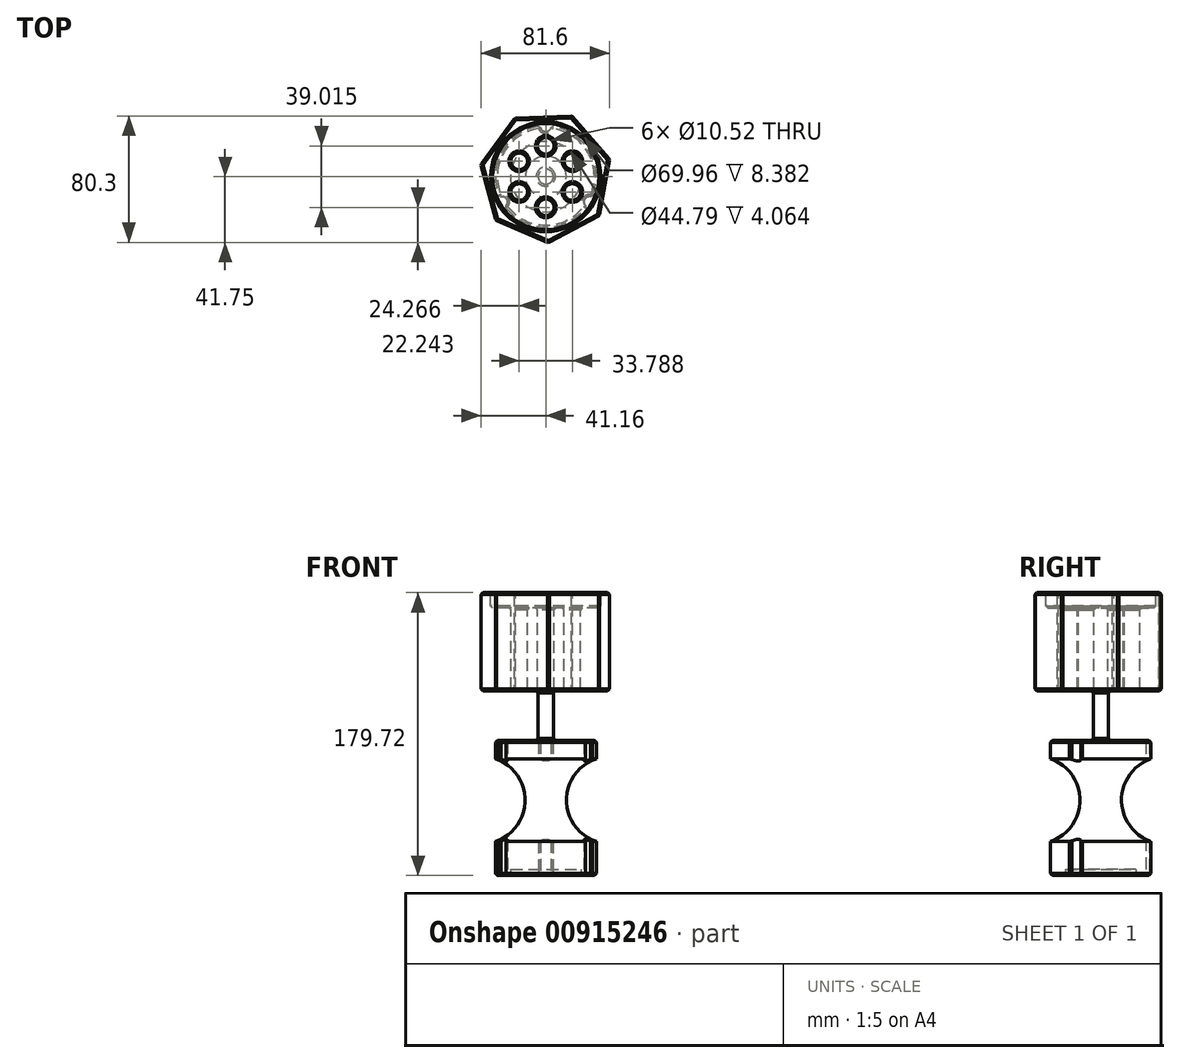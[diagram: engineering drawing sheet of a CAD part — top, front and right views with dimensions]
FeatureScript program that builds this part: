
annotation { "Feature Type Name" : "Feature", "Feature Type Description" : "" }
export const myFeature = defineFeature(function(context is Context, id is Id, definition is map)
    precondition{}
    {
        {
            var Q0;
            Q0=qCreatedBy(makeId("Front.planeOp"),FACE);
            var sketch = newSketch(context, id + "F0", { "sketchPlane" : qUnion([Q0])});
            skLineSegment(sketch, "E0.bottom", {"start": v(0, 38.08) * mm, "end": v(32.08, 38.08) * mm});
            skLineSegment(sketch, "E0.top", {"start": v(0, -47.91) * mm, "end": v(32.08, -47.91) * mm});
            skLineSegment(sketch, "E0.left", {"start": v(0, 38.08) * mm, "end": v(0, -47.91) * mm});
            skLineSegment(sketch, "E0.right", {"start": v(32.08, 38.08) * mm, "end": v(32.08, -47.91) * mm});
            skLineSegment(sketch, "E1", {"start": v(0, 0) * mm, "end": v(0, 52.01) * mm, "construction": true});
            skLineSegment(sketch, "E2", {"start": v(0, 0) * mm, "end": v(0, -67.99) * mm, "construction": true});
            skSolve(sketch);
        }
        {
            var Q0;
            Q0 = qSketchRegion(id + "F0", true);
            var Q1;
            Q1=sQuery(id+"F0.wireOp",EDGE,"E1");
            revolve(context, id + "F1", {"surfaceOperationType" : NewSurfaceOperationType.NEW, "entities" : qUnion([Q0]), "axis" : qUnion([Q1]), "revolveType" : RevolveType.FULL});
        }
        {
            var Q0;
            Q0=makeQuery(id+"F1.opRevolve","SWEPT_FACE",FACE,{"disambiguationData":[OSD([sQuery(id+"F0.wireOp",EDGE,"E0.bottom")])]});
            var sketch = newSketch(context, id + "F2", { "sketchPlane" : qUnion([Q0])});
            skCircle(sketch, "E3", {"center": v(0, 0) * mm, "radius": 4.8 * mm});
            skSolve(sketch);
        }
        {
            var Q0;
            Q0 = qSketchRegion(id + "F2", true);
            extrude(context, id + "F3", {"entities" : qUnion([Q0]), "operationType" : NewBodyOperationType.ADD, "depth" : 93.73 * mm, "offsetDistance" : 25.4 * mm});
        }
        {
            var Q0;
            Q0=makeQuery(id+"F3.opExtrude","CAP_FACE",FACE,{"disambiguationData":[OSD([sQuery(id+"F2.wireOp",EDGE,"E3")])],"isStart":false});
            var sketch = newSketch(context, id + "F4", { "sketchPlane" : qUnion([Q0])});
            skCircle(sketch, "E4.cCircle", {"center": v(0, 0) * mm, "radius": 37.86 * mm, "construction": true});
            skLineSegment(sketch, "E4.0", {"start": v(40.55, 11.03) * mm, "end": v(33.9, -24.83) * mm});
            skLineSegment(sketch, "E4.1", {"start": v(33.9, -24.83) * mm, "end": v(1.73, -41.99) * mm});
            skLineSegment(sketch, "E4.2", {"start": v(1.73, -41.99) * mm, "end": v(-31.75, -27.53) * mm});
            skLineSegment(sketch, "E4.3", {"start": v(-31.75, -27.53) * mm, "end": v(-41.32, 7.66) * mm});
            skLineSegment(sketch, "E4.4", {"start": v(-41.32, 7.66) * mm, "end": v(-19.78, 37.08) * mm});
            skLineSegment(sketch, "E4.5", {"start": v(-19.78, 37.08) * mm, "end": v(16.66, 38.58) * mm});
            skLineSegment(sketch, "E4.6", {"start": v(16.66, 38.58) * mm, "end": v(40.55, 11.03) * mm});
            skPoint(sketch, "E4.0.midPoint", {"position": v(37.23, -6.9) * mm});
            skSolve(sketch);
        }
        {
            var Q0;
            Q0 = qSketchRegion(id + "F4", true);
            extrude(context, id + "F5", {"entities" : qUnion([Q0]), "operationType" : NewBodyOperationType.ADD, "oppositeDirection" : true, "depth" : 62.48 * mm, "offsetDistance" : 25.4 * mm});
        }
        {
            var Q0;
            Q0=makeQuery(id+"F5.boolean.opBoolean","MERGE",FACE,{"derivedFrom":[makeQuery(id+"F3.opExtrude","CAP_FACE",FACE,{"disambiguationData":[OSD([sQuery(id+"F2.wireOp",EDGE,"E3")])],"isStart":false}),makeQuery(id+"F5.opExtrude","CAP_FACE",FACE,{"disambiguationData":[OSD([sQuery(id+"F4.wireOp",EDGE,"E4.0"),sQuery(id+"F4.wireOp",EDGE,"E4.1"),sQuery(id+"F4.wireOp",EDGE,"E4.2"),sQuery(id+"F4.wireOp",EDGE,"E4.3"),sQuery(id+"F4.wireOp",EDGE,"E4.4"),sQuery(id+"F4.wireOp",EDGE,"E4.5"),sQuery(id+"F4.wireOp",EDGE,"E4.6")])],"isStart":true})]});
            var sketch = newSketch(context, id + "F6", { "sketchPlane" : qUnion([Q0])});
            skCircle(sketch, "E5", {"center": v(0, 0) * mm, "radius": 34.98 * mm});
            skSolve(sketch);
        }
        {
            var Q0;
            Q0 = qSketchRegion(id + "F6", true);
            extrude(context, id + "F7", {"entities" : qUnion([Q0]), "operationType" : NewBodyOperationType.REMOVE, "oppositeDirection" : true, "depth" : 9.65 * mm, "offsetDistance" : 25.4 * mm});
        }
        {
            var Q0;
            Q0=makeQuery(id+"F7.boolean.opBoolean","COPY",FACE,{"derivedFrom":makeQuery(id+"F7.opExtrude","CAP_FACE",FACE,{"disambiguationData":[OSD([sQuery(id+"F6.wireOp",EDGE,"E5")])],"isStart":false})});
            var sketch = newSketch(context, id + "F8", { "sketchPlane" : qUnion([Q0])});
            skCircle(sketch, "E6", {"center": v(0, 19.5) * mm, "radius": 5.26 * mm});
            skCircle(sketch, "E7.1.0", {"center": v(-16.9, 9.75) * mm, "radius": 5.26 * mm});
            skCircle(sketch, "E7.2.0", {"center": v(-16.9, -9.75) * mm, "radius": 5.26 * mm});
            skCircle(sketch, "E7.3.0", {"center": v(0, -19.5) * mm, "radius": 5.26 * mm});
            skCircle(sketch, "E7.4.0", {"center": v(16.9, -9.75) * mm, "radius": 5.26 * mm});
            skCircle(sketch, "E7.5.0", {"center": v(16.9, 9.75) * mm, "radius": 5.26 * mm});
            skPoint(sketch, "E7.center", {"position": v(0, 0) * mm});
            skSolve(sketch);
        }
        {
            var Q0;
            Q0=makeQuery(id+"F8.imprint","IMPRINT",FACE,{"disambiguationData":[TD([[makeQuery(id+"F8.imprint","IMPRINT",EDGE,{"derivedFrom":sQuery(id+"F8.wireOp",EDGE,"E7.1.0")}),1.0]])]});
            var Q1;
            Q1=makeQuery(id+"F8.imprint","IMPRINT",FACE,{"disambiguationData":[TD([[makeQuery(id+"F8.imprint","IMPRINT",EDGE,{"derivedFrom":sQuery(id+"F8.wireOp",EDGE,"E6")}),1.0]])]});
            var Q2;
            Q2=makeQuery(id+"F8.imprint","IMPRINT",FACE,{"disambiguationData":[TD([[makeQuery(id+"F8.imprint","IMPRINT",EDGE,{"derivedFrom":sQuery(id+"F8.wireOp",EDGE,"E7.5.0")}),1.0]])]});
            var Q3;
            Q3=makeQuery(id+"F8.imprint","IMPRINT",FACE,{"disambiguationData":[TD([[makeQuery(id+"F8.imprint","IMPRINT",EDGE,{"derivedFrom":sQuery(id+"F8.wireOp",EDGE,"E7.4.0")}),1.0]])]});
            var Q4;
            Q4=makeQuery(id+"F8.imprint","IMPRINT",FACE,{"disambiguationData":[TD([[makeQuery(id+"F8.imprint","IMPRINT",EDGE,{"derivedFrom":sQuery(id+"F8.wireOp",EDGE,"E7.3.0")}),1.0]])]});
            var Q5;
            Q5=makeQuery(id+"F8.imprint","IMPRINT",FACE,{"disambiguationData":[TD([[makeQuery(id+"F8.imprint","IMPRINT",EDGE,{"derivedFrom":sQuery(id+"F8.wireOp",EDGE,"E7.2.0")}),1.0]])]});
            extrude(context, id + "F9", {"entities" : qUnion([Q0, Q1, Q2, Q3, Q4, Q5]), "operationType" : NewBodyOperationType.REMOVE, "oppositeDirection" : true, "depth" : 74.17 * mm, "offsetDistance" : 25.4 * mm});
        }
        {
            var Q0;
            Q0=makeQuery(id+"F1.opRevolve","SWEPT_FACE",FACE,{"disambiguationData":[OSD([sQuery(id+"F0.wireOp",EDGE,"E0.top")])]});
            var sketch = newSketch(context, id + "F10", { "sketchPlane" : qUnion([Q0])});
            skCircle(sketch, "E8", {"center": v(0, -32.08) * mm, "radius": 3.46 * mm});
            skCircle(sketch, "E9.1.0", {"center": v(27.78, 16.04) * mm, "radius": 3.46 * mm});
            skCircle(sketch, "E9.2.0", {"center": v(-27.78, 16.04) * mm, "radius": 3.46 * mm});
            skPoint(sketch, "E9.center", {"position": v(0, 0) * mm});
            skSolve(sketch);
        }
        {
            var Q0;
            Q0 = qSketchRegion(id + "F10", true);
            extrude(context, id + "F11", {"entities" : qUnion([Q0]), "operationType" : NewBodyOperationType.REMOVE, "oppositeDirection" : true, "depth" : 91.19 * mm, "offsetDistance" : 25.4 * mm});
        }
        {
            var Q0;
            Q0=makeQuery(id+"F5.opExtrude","CAP_FACE",FACE,{"disambiguationData":[OSD([sQuery(id+"F4.wireOp",EDGE,"E4.0"),sQuery(id+"F4.wireOp",EDGE,"E4.1"),sQuery(id+"F4.wireOp",EDGE,"E4.2"),sQuery(id+"F4.wireOp",EDGE,"E4.3"),sQuery(id+"F4.wireOp",EDGE,"E4.4"),sQuery(id+"F4.wireOp",EDGE,"E4.5"),sQuery(id+"F4.wireOp",EDGE,"E4.6")])],"isStart":false});
            var Q1;
            Q1=makeQuery(id+"F1.opRevolve","SWEPT_FACE",FACE,{"disambiguationData":[OSD([sQuery(id+"F0.wireOp",EDGE,"E0.top")])]});
            var Q2;
            Q2=makeQuery(id+"F7.boolean.opBoolean","COPY",FACE,{"derivedFrom":makeQuery(id+"F7.opExtrude","CAP_FACE",FACE,{"disambiguationData":[OSD([sQuery(id+"F6.wireOp",EDGE,"E5")])],"isStart":false})});
            var Q3;
            Q3=makeQuery(id+"F7.boolean.opBoolean","COPY",EDGE,{"derivedFrom":makeQuery(id+"F7.opExtrude","CAP_EDGE",EDGE,{"disambiguationData":[OSD([sQuery(id+"F6.wireOp",EDGE,"E5")])],"isStart":true})});
            var Q4;
            Q4=makeQuery(id+"F5.opExtrude","CAP_EDGE",EDGE,{"disambiguationData":[OSD([sQuery(id+"F4.wireOp",EDGE,"E4.6")])],"isStart":true});
            var Q5;
            Q5=makeQuery(id+"F5.opExtrude","CAP_EDGE",EDGE,{"disambiguationData":[OSD([sQuery(id+"F4.wireOp",EDGE,"E4.5")])],"isStart":true});
            var Q6;
            Q6=makeQuery(id+"F5.opExtrude","CAP_EDGE",EDGE,{"disambiguationData":[OSD([sQuery(id+"F4.wireOp",EDGE,"E4.0")])],"isStart":true});
            var Q7;
            Q7=makeQuery(id+"F5.opExtrude","CAP_EDGE",EDGE,{"disambiguationData":[OSD([sQuery(id+"F4.wireOp",EDGE,"E4.1")])],"isStart":true});
            var Q8;
            Q8=makeQuery(id+"F5.opExtrude","CAP_EDGE",EDGE,{"disambiguationData":[OSD([sQuery(id+"F4.wireOp",EDGE,"E4.2")])],"isStart":true});
            var Q9;
            Q9=makeQuery(id+"F5.opExtrude","CAP_EDGE",EDGE,{"disambiguationData":[OSD([sQuery(id+"F4.wireOp",EDGE,"E4.3")])],"isStart":true});
            var Q10;
            Q10=makeQuery(id+"F5.opExtrude","CAP_EDGE",EDGE,{"disambiguationData":[OSD([sQuery(id+"F4.wireOp",EDGE,"E4.4")])],"isStart":true});
            var Q11;
            {var subQ0=sQuery(id+"F0.wireOp",EDGE,"E0.bottom");var subQ1=sQuery(id+"F0.wireOp",EDGE,"E0.right");Q11=makeQuery(id+"F11.boolean.opBoolean","SPLIT",EDGE,{"disambiguationData":[TD([makeQuery(id+"F1.opRevolve","SWEPT_FACE",FACE,{"disambiguationData":[OSD([subQ0])]}),makeQuery(id+"F1.opRevolve","SWEPT_FACE",FACE,{"disambiguationData":[OSD([subQ1])]}),makeQuery(id+"F11.opExtrude","SWEPT_FACE",FACE,{"disambiguationData":[OSD([sQuery(id+"F10.wireOp",EDGE,"E9.1.0")])]}),makeQuery(id+"F11.opExtrude","SWEPT_FACE",FACE,{"disambiguationData":[OSD([sQuery(id+"F10.wireOp",EDGE,"E9.2.0")])]})])],"derivedFrom":makeQuery(id+"F1.opRevolve","SWEPT_EDGE",EDGE,{"disambiguationData":[OSD([subQ0,subQ1])]})});}
            var Q12;
            Q12=makeQuery(id+"F11.boolean.opBoolean","INTERSECT",EDGE,{"derivedFrom":[makeQuery(id+"F1.opRevolve","SWEPT_FACE",FACE,{"disambiguationData":[OSD([sQuery(id+"F0.wireOp",EDGE,"E0.bottom")])]}),makeQuery(id+"F11.opExtrude","SWEPT_FACE",FACE,{"disambiguationData":[OSD([sQuery(id+"F10.wireOp",EDGE,"E9.2.0")])]})]});
            var Q13;
            Q13=makeQuery(id+"F1.opRevolve","SWEPT_FACE",FACE,{"disambiguationData":[OSD([sQuery(id+"F0.wireOp",EDGE,"E0.bottom")])]});
            var Q14;
            Q14=makeQuery(id+"F9.boolean.opBoolean","COPY",EDGE,{"derivedFrom":makeQuery(id+"F9.opExtrude","CAP_EDGE",EDGE,{"disambiguationData":[OSD([sQuery(id+"F8.wireOp",EDGE,"E7.2.0")])],"isStart":true})});
            var Q15;
            Q15=makeQuery(id+"F5.opExtrude","CAP_EDGE",EDGE,{"disambiguationData":[OSD([sQuery(id+"F4.wireOp",EDGE,"E4.4")])],"isStart":false});
            var Q16;
            Q16=makeQuery(id+"F5.opExtrude","SWEPT_EDGE",EDGE,{"disambiguationData":[OSD([sQuery(id+"F4.wireOp",EDGE,"E4.4"),sQuery(id+"F4.wireOp",EDGE,"E4.5")])]});
            var Q17;
            Q17=makeQuery(id+"F5.opExtrude","SWEPT_EDGE",EDGE,{"disambiguationData":[OSD([sQuery(id+"F4.wireOp",EDGE,"E4.2"),sQuery(id+"F4.wireOp",EDGE,"E4.3")])]});
            var Q18;
            Q18=makeQuery(id+"F5.opExtrude","SWEPT_EDGE",EDGE,{"disambiguationData":[OSD([sQuery(id+"F4.wireOp",EDGE,"E4.1"),sQuery(id+"F4.wireOp",EDGE,"E4.2")])]});
            var Q19;
            Q19=makeQuery(id+"F9.boolean.opBoolean","COPY",EDGE,{"derivedFrom":makeQuery(id+"F9.opExtrude","CAP_EDGE",EDGE,{"disambiguationData":[OSD([sQuery(id+"F8.wireOp",EDGE,"E7.5.0")])],"isStart":true})});
            var Q20;
            Q20=makeQuery(id+"F9.boolean.opBoolean","COPY",EDGE,{"derivedFrom":makeQuery(id+"F9.opExtrude","CAP_EDGE",EDGE,{"disambiguationData":[OSD([sQuery(id+"F8.wireOp",EDGE,"E7.4.0")])],"isStart":true})});
            var Q21;
            Q21=makeQuery(id+"F9.boolean.opBoolean","COPY",EDGE,{"derivedFrom":makeQuery(id+"F9.opExtrude","CAP_EDGE",EDGE,{"disambiguationData":[OSD([sQuery(id+"F8.wireOp",EDGE,"E6")])],"isStart":true})});
            var Q22;
            {var subQ0=sQuery(id+"F0.wireOp",EDGE,"E0.bottom");var subQ1=sQuery(id+"F0.wireOp",EDGE,"E0.right");Q22=makeQuery(id+"F11.boolean.opBoolean","SPLIT",EDGE,{"disambiguationData":[TD([makeQuery(id+"F1.opRevolve","SWEPT_FACE",FACE,{"disambiguationData":[OSD([subQ0])]}),makeQuery(id+"F1.opRevolve","SWEPT_FACE",FACE,{"disambiguationData":[OSD([subQ1])]}),makeQuery(id+"F11.opExtrude","SWEPT_FACE",FACE,{"disambiguationData":[OSD([sQuery(id+"F10.wireOp",EDGE,"E8")])]}),makeQuery(id+"F11.opExtrude","SWEPT_FACE",FACE,{"disambiguationData":[OSD([sQuery(id+"F10.wireOp",EDGE,"E9.2.0")])]})])],"derivedFrom":makeQuery(id+"F1.opRevolve","SWEPT_EDGE",EDGE,{"disambiguationData":[OSD([subQ0,subQ1])]})});}
            var Q23;
            Q23=makeQuery(id+"F7.boolean.opBoolean","COPY",EDGE,{"derivedFrom":makeQuery(id+"F7.opExtrude","CAP_EDGE",EDGE,{"disambiguationData":[OSD([sQuery(id+"F6.wireOp",EDGE,"E5")])],"isStart":false})});
            var Q24;
            Q24=makeQuery(id+"F9.boolean.opBoolean","COPY",EDGE,{"derivedFrom":makeQuery(id+"F9.opExtrude","CAP_EDGE",EDGE,{"disambiguationData":[OSD([sQuery(id+"F8.wireOp",EDGE,"E7.3.0")])],"isStart":true})});
            var Q25;
            Q25=makeQuery(id+"F9.boolean.opBoolean","INTERSECT",EDGE,{"derivedFrom":[makeQuery(id+"F5.opExtrude","CAP_FACE",FACE,{"disambiguationData":[OSD([sQuery(id+"F4.wireOp",EDGE,"E4.0"),sQuery(id+"F4.wireOp",EDGE,"E4.1"),sQuery(id+"F4.wireOp",EDGE,"E4.2"),sQuery(id+"F4.wireOp",EDGE,"E4.3"),sQuery(id+"F4.wireOp",EDGE,"E4.4"),sQuery(id+"F4.wireOp",EDGE,"E4.5"),sQuery(id+"F4.wireOp",EDGE,"E4.6")])],"isStart":false}),makeQuery(id+"F9.opExtrude","SWEPT_FACE",FACE,{"disambiguationData":[OSD([sQuery(id+"F8.wireOp",EDGE,"E6")])]})]});
            var Q26;
            Q26=makeQuery(id+"F9.boolean.opBoolean","INTERSECT",EDGE,{"derivedFrom":[makeQuery(id+"F5.opExtrude","CAP_FACE",FACE,{"disambiguationData":[OSD([sQuery(id+"F4.wireOp",EDGE,"E4.0"),sQuery(id+"F4.wireOp",EDGE,"E4.1"),sQuery(id+"F4.wireOp",EDGE,"E4.2"),sQuery(id+"F4.wireOp",EDGE,"E4.3"),sQuery(id+"F4.wireOp",EDGE,"E4.4"),sQuery(id+"F4.wireOp",EDGE,"E4.5"),sQuery(id+"F4.wireOp",EDGE,"E4.6")])],"isStart":false}),makeQuery(id+"F9.opExtrude","SWEPT_FACE",FACE,{"disambiguationData":[OSD([sQuery(id+"F8.wireOp",EDGE,"E7.3.0")])]})]});
            var Q27;
            Q27=makeQuery(id+"F5.opExtrude","SWEPT_EDGE",EDGE,{"disambiguationData":[OSD([sQuery(id+"F4.wireOp",EDGE,"E4.0"),sQuery(id+"F4.wireOp",EDGE,"E4.1")])]});
            var Q28;
            Q28=makeQuery(id+"F5.opExtrude","CAP_EDGE",EDGE,{"disambiguationData":[OSD([sQuery(id+"F4.wireOp",EDGE,"E4.5")])],"isStart":false});
            var Q29;
            {var subQ0=sQuery(id+"F0.wireOp",EDGE,"E0.top");var subQ1=sQuery(id+"F0.wireOp",EDGE,"E0.right");Q29=makeQuery(id+"F11.boolean.opBoolean","SPLIT",EDGE,{"disambiguationData":[TD([makeQuery(id+"F1.opRevolve","SWEPT_FACE",FACE,{"disambiguationData":[OSD([subQ0])]}),makeQuery(id+"F1.opRevolve","SWEPT_FACE",FACE,{"disambiguationData":[OSD([subQ1])]}),makeQuery(id+"F11.opExtrude","SWEPT_FACE",FACE,{"disambiguationData":[OSD([sQuery(id+"F10.wireOp",EDGE,"E9.1.0")])]}),makeQuery(id+"F11.opExtrude","SWEPT_FACE",FACE,{"disambiguationData":[OSD([sQuery(id+"F10.wireOp",EDGE,"E9.2.0")])]})])],"derivedFrom":makeQuery(id+"F1.opRevolve","SWEPT_EDGE",EDGE,{"disambiguationData":[OSD([subQ0,subQ1])]})});}
            var Q30;
            Q30=makeQuery(id+"F5.opExtrude","CAP_EDGE",EDGE,{"disambiguationData":[OSD([sQuery(id+"F4.wireOp",EDGE,"E4.6")])],"isStart":false});
            var Q31;
            Q31=makeQuery(id+"F11.boolean.opBoolean","INTERSECT",EDGE,{"disambiguationData":[OD(1.0)],"derivedFrom":[makeQuery(id+"F1.opRevolve","SWEPT_FACE",FACE,{"disambiguationData":[OSD([sQuery(id+"F0.wireOp",EDGE,"E0.right")])]}),makeQuery(id+"F11.opExtrude","SWEPT_FACE",FACE,{"disambiguationData":[OSD([sQuery(id+"F10.wireOp",EDGE,"E9.2.0")])]})]});
            var Q32;
            {var subQ0=sQuery(id+"F0.wireOp",EDGE,"E0.top");var subQ1=sQuery(id+"F0.wireOp",EDGE,"E0.right");Q32=makeQuery(id+"F11.boolean.opBoolean","SPLIT",EDGE,{"disambiguationData":[TD([makeQuery(id+"F1.opRevolve","SWEPT_FACE",FACE,{"disambiguationData":[OSD([subQ0])]}),makeQuery(id+"F1.opRevolve","SWEPT_FACE",FACE,{"disambiguationData":[OSD([subQ1])]}),makeQuery(id+"F11.opExtrude","SWEPT_FACE",FACE,{"disambiguationData":[OSD([sQuery(id+"F10.wireOp",EDGE,"E8")])]}),makeQuery(id+"F11.opExtrude","SWEPT_FACE",FACE,{"disambiguationData":[OSD([sQuery(id+"F10.wireOp",EDGE,"E9.2.0")])]})])],"derivedFrom":makeQuery(id+"F1.opRevolve","SWEPT_EDGE",EDGE,{"disambiguationData":[OSD([subQ0,subQ1])]})});}
            var Q33;
            Q33=makeQuery(id+"F11.boolean.opBoolean","INTERSECT",EDGE,{"derivedFrom":[makeQuery(id+"F1.opRevolve","SWEPT_FACE",FACE,{"disambiguationData":[OSD([sQuery(id+"F0.wireOp",EDGE,"E0.bottom")])]}),makeQuery(id+"F11.opExtrude","SWEPT_FACE",FACE,{"disambiguationData":[OSD([sQuery(id+"F10.wireOp",EDGE,"E8")])]})]});
            var Q34;
            Q34=makeQuery(id+"F5.opExtrude","CAP_EDGE",EDGE,{"disambiguationData":[OSD([sQuery(id+"F4.wireOp",EDGE,"E4.0")])],"isStart":false});
            var Q35;
            Q35=makeQuery(id+"F5.opExtrude","CAP_EDGE",EDGE,{"disambiguationData":[OSD([sQuery(id+"F4.wireOp",EDGE,"E4.1")])],"isStart":false});
            var Q36;
            {var subQ0=sQuery(id+"F0.wireOp",EDGE,"E0.bottom");var subQ1=sQuery(id+"F0.wireOp",EDGE,"E0.right");Q36=makeQuery(id+"F11.boolean.opBoolean","SPLIT",EDGE,{"disambiguationData":[TD([makeQuery(id+"F1.opRevolve","SWEPT_FACE",FACE,{"disambiguationData":[OSD([subQ0])]}),makeQuery(id+"F1.opRevolve","SWEPT_FACE",FACE,{"disambiguationData":[OSD([subQ1])]}),makeQuery(id+"F11.opExtrude","SWEPT_FACE",FACE,{"disambiguationData":[OSD([sQuery(id+"F10.wireOp",EDGE,"E8")])]}),makeQuery(id+"F11.opExtrude","SWEPT_FACE",FACE,{"disambiguationData":[OSD([sQuery(id+"F10.wireOp",EDGE,"E9.1.0")])]})])],"derivedFrom":makeQuery(id+"F1.opRevolve","SWEPT_EDGE",EDGE,{"disambiguationData":[OSD([subQ0,subQ1])]})});}
            var Q37;
            Q37=makeQuery(id+"F5.opExtrude","SWEPT_EDGE",EDGE,{"disambiguationData":[OSD([sQuery(id+"F4.wireOp",EDGE,"E4.5"),sQuery(id+"F4.wireOp",EDGE,"E4.6")])]});
            var Q38;
            Q38=makeQuery(id+"F5.opExtrude","SWEPT_EDGE",EDGE,{"disambiguationData":[OSD([sQuery(id+"F4.wireOp",EDGE,"E4.0"),sQuery(id+"F4.wireOp",EDGE,"E4.6")])]});
            var Q39;
            Q39=makeQuery(id+"F5.opExtrude","CAP_EDGE",EDGE,{"disambiguationData":[OSD([sQuery(id+"F4.wireOp",EDGE,"E4.3")])],"isStart":false});
            var Q40;
            Q40=makeQuery(id+"F5.opExtrude","SWEPT_EDGE",EDGE,{"disambiguationData":[OSD([sQuery(id+"F4.wireOp",EDGE,"E4.3"),sQuery(id+"F4.wireOp",EDGE,"E4.4")])]});
            var Q41;
            Q41=makeQuery(id+"F9.boolean.opBoolean","INTERSECT",EDGE,{"derivedFrom":[makeQuery(id+"F5.opExtrude","CAP_FACE",FACE,{"disambiguationData":[OSD([sQuery(id+"F4.wireOp",EDGE,"E4.0"),sQuery(id+"F4.wireOp",EDGE,"E4.1"),sQuery(id+"F4.wireOp",EDGE,"E4.2"),sQuery(id+"F4.wireOp",EDGE,"E4.3"),sQuery(id+"F4.wireOp",EDGE,"E4.4"),sQuery(id+"F4.wireOp",EDGE,"E4.5"),sQuery(id+"F4.wireOp",EDGE,"E4.6")])],"isStart":false}),makeQuery(id+"F9.opExtrude","SWEPT_FACE",FACE,{"disambiguationData":[OSD([sQuery(id+"F8.wireOp",EDGE,"E7.4.0")])]})]});
            var Q42;
            Q42=makeQuery(id+"F9.boolean.opBoolean","INTERSECT",EDGE,{"derivedFrom":[makeQuery(id+"F5.opExtrude","CAP_FACE",FACE,{"disambiguationData":[OSD([sQuery(id+"F4.wireOp",EDGE,"E4.0"),sQuery(id+"F4.wireOp",EDGE,"E4.1"),sQuery(id+"F4.wireOp",EDGE,"E4.2"),sQuery(id+"F4.wireOp",EDGE,"E4.3"),sQuery(id+"F4.wireOp",EDGE,"E4.4"),sQuery(id+"F4.wireOp",EDGE,"E4.5"),sQuery(id+"F4.wireOp",EDGE,"E4.6")])],"isStart":false}),makeQuery(id+"F9.opExtrude","SWEPT_FACE",FACE,{"disambiguationData":[OSD([sQuery(id+"F8.wireOp",EDGE,"E7.1.0")])]})]});
            var Q43;
            Q43=makeQuery(id+"F9.boolean.opBoolean","COPY",EDGE,{"derivedFrom":makeQuery(id+"F9.opExtrude","CAP_EDGE",EDGE,{"disambiguationData":[OSD([sQuery(id+"F8.wireOp",EDGE,"E7.1.0")])],"isStart":true})});
            var Q44;
            Q44=makeQuery(id+"F5.opExtrude","CAP_EDGE",EDGE,{"disambiguationData":[OSD([sQuery(id+"F4.wireOp",EDGE,"E4.2")])],"isStart":false});
            var Q45;
            Q45=makeQuery(id+"F5.boolean.opBoolean","INTERSECT",EDGE,{"derivedFrom":[makeQuery(id+"F3.opExtrude","SWEPT_FACE",FACE,{"disambiguationData":[OSD([sQuery(id+"F2.wireOp",EDGE,"E3")])]}),makeQuery(id+"F5.opExtrude","CAP_FACE",FACE,{"disambiguationData":[OSD([sQuery(id+"F4.wireOp",EDGE,"E4.0"),sQuery(id+"F4.wireOp",EDGE,"E4.1"),sQuery(id+"F4.wireOp",EDGE,"E4.2"),sQuery(id+"F4.wireOp",EDGE,"E4.3"),sQuery(id+"F4.wireOp",EDGE,"E4.4"),sQuery(id+"F4.wireOp",EDGE,"E4.5"),sQuery(id+"F4.wireOp",EDGE,"E4.6")])],"isStart":false})]});
            var Q46;
            Q46=makeQuery(id+"F11.boolean.opBoolean","INTERSECT",EDGE,{"disambiguationData":[OD(0.0)],"derivedFrom":[makeQuery(id+"F1.opRevolve","SWEPT_FACE",FACE,{"disambiguationData":[OSD([sQuery(id+"F0.wireOp",EDGE,"E0.right")])]}),makeQuery(id+"F11.opExtrude","SWEPT_FACE",FACE,{"disambiguationData":[OSD([sQuery(id+"F10.wireOp",EDGE,"E9.2.0")])]})]});
            var Q47;
            Q47=makeQuery(id+"F9.boolean.opBoolean","INTERSECT",EDGE,{"derivedFrom":[makeQuery(id+"F5.opExtrude","CAP_FACE",FACE,{"disambiguationData":[OSD([sQuery(id+"F4.wireOp",EDGE,"E4.0"),sQuery(id+"F4.wireOp",EDGE,"E4.1"),sQuery(id+"F4.wireOp",EDGE,"E4.2"),sQuery(id+"F4.wireOp",EDGE,"E4.3"),sQuery(id+"F4.wireOp",EDGE,"E4.4"),sQuery(id+"F4.wireOp",EDGE,"E4.5"),sQuery(id+"F4.wireOp",EDGE,"E4.6")])],"isStart":false}),makeQuery(id+"F9.opExtrude","SWEPT_FACE",FACE,{"disambiguationData":[OSD([sQuery(id+"F8.wireOp",EDGE,"E7.2.0")])]})]});
            var Q48;
            Q48=makeQuery(id+"F9.boolean.opBoolean","INTERSECT",EDGE,{"derivedFrom":[makeQuery(id+"F5.opExtrude","CAP_FACE",FACE,{"disambiguationData":[OSD([sQuery(id+"F4.wireOp",EDGE,"E4.0"),sQuery(id+"F4.wireOp",EDGE,"E4.1"),sQuery(id+"F4.wireOp",EDGE,"E4.2"),sQuery(id+"F4.wireOp",EDGE,"E4.3"),sQuery(id+"F4.wireOp",EDGE,"E4.4"),sQuery(id+"F4.wireOp",EDGE,"E4.5"),sQuery(id+"F4.wireOp",EDGE,"E4.6")])],"isStart":false}),makeQuery(id+"F9.opExtrude","SWEPT_FACE",FACE,{"disambiguationData":[OSD([sQuery(id+"F8.wireOp",EDGE,"E7.5.0")])]})]});
            var Q49;
            Q49=makeQuery(id+"F11.boolean.opBoolean","INTERSECT",EDGE,{"disambiguationData":[OD(0.0)],"derivedFrom":[makeQuery(id+"F1.opRevolve","SWEPT_FACE",FACE,{"disambiguationData":[OSD([sQuery(id+"F0.wireOp",EDGE,"E0.right")])]}),makeQuery(id+"F11.opExtrude","SWEPT_FACE",FACE,{"disambiguationData":[OSD([sQuery(id+"F10.wireOp",EDGE,"E8")])]})]});
            var Q50;
            Q50=makeQuery(id+"F11.boolean.opBoolean","INTERSECT",EDGE,{"disambiguationData":[OD(1.0)],"derivedFrom":[makeQuery(id+"F1.opRevolve","SWEPT_FACE",FACE,{"disambiguationData":[OSD([sQuery(id+"F0.wireOp",EDGE,"E0.right")])]}),makeQuery(id+"F11.opExtrude","SWEPT_FACE",FACE,{"disambiguationData":[OSD([sQuery(id+"F10.wireOp",EDGE,"E8")])]})]});
            var Q51;
            Q51=makeQuery(id+"F11.boolean.opBoolean","COPY",EDGE,{"derivedFrom":makeQuery(id+"F11.opExtrude","CAP_EDGE",EDGE,{"disambiguationData":[OSD([sQuery(id+"F10.wireOp",EDGE,"E9.2.0")])],"isStart":true})});
            var Q52;
            Q52=makeQuery(id+"F3.opExtrude","CAP_EDGE",EDGE,{"disambiguationData":[OSD([sQuery(id+"F2.wireOp",EDGE,"E3")])],"isStart":true});
            var Q53;
            {var subQ0=sQuery(id+"F0.wireOp",EDGE,"E0.top");var subQ1=sQuery(id+"F0.wireOp",EDGE,"E0.right");Q53=makeQuery(id+"F11.boolean.opBoolean","SPLIT",EDGE,{"disambiguationData":[TD([makeQuery(id+"F1.opRevolve","SWEPT_FACE",FACE,{"disambiguationData":[OSD([subQ0])]}),makeQuery(id+"F1.opRevolve","SWEPT_FACE",FACE,{"disambiguationData":[OSD([subQ1])]}),makeQuery(id+"F11.opExtrude","SWEPT_FACE",FACE,{"disambiguationData":[OSD([sQuery(id+"F10.wireOp",EDGE,"E8")])]}),makeQuery(id+"F11.opExtrude","SWEPT_FACE",FACE,{"disambiguationData":[OSD([sQuery(id+"F10.wireOp",EDGE,"E9.1.0")])]})])],"derivedFrom":makeQuery(id+"F1.opRevolve","SWEPT_EDGE",EDGE,{"disambiguationData":[OSD([subQ0,subQ1])]})});}
            var Q54;
            Q54=makeQuery(id+"F11.boolean.opBoolean","COPY",EDGE,{"derivedFrom":makeQuery(id+"F11.opExtrude","CAP_EDGE",EDGE,{"disambiguationData":[OSD([sQuery(id+"F10.wireOp",EDGE,"E8")])],"isStart":true})});
            var Q55;
            Q55=makeQuery(id+"F11.boolean.opBoolean","INTERSECT",EDGE,{"disambiguationData":[OD(1.0)],"derivedFrom":[makeQuery(id+"F1.opRevolve","SWEPT_FACE",FACE,{"disambiguationData":[OSD([sQuery(id+"F0.wireOp",EDGE,"E0.right")])]}),makeQuery(id+"F11.opExtrude","SWEPT_FACE",FACE,{"disambiguationData":[OSD([sQuery(id+"F10.wireOp",EDGE,"E9.1.0")])]})]});
            var Q56;
            Q56=makeQuery(id+"F11.boolean.opBoolean","COPY",EDGE,{"derivedFrom":makeQuery(id+"F11.opExtrude","CAP_EDGE",EDGE,{"disambiguationData":[OSD([sQuery(id+"F10.wireOp",EDGE,"E9.1.0")])],"isStart":true})});
            var Q57;
            Q57=makeQuery(id+"F11.boolean.opBoolean","INTERSECT",EDGE,{"derivedFrom":[makeQuery(id+"F1.opRevolve","SWEPT_FACE",FACE,{"disambiguationData":[OSD([sQuery(id+"F0.wireOp",EDGE,"E0.bottom")])]}),makeQuery(id+"F11.opExtrude","SWEPT_FACE",FACE,{"disambiguationData":[OSD([sQuery(id+"F10.wireOp",EDGE,"E9.1.0")])]})]});
            var Q58;
            Q58=makeQuery(id+"F11.boolean.opBoolean","INTERSECT",EDGE,{"disambiguationData":[OD(0.0)],"derivedFrom":[makeQuery(id+"F1.opRevolve","SWEPT_FACE",FACE,{"disambiguationData":[OSD([sQuery(id+"F0.wireOp",EDGE,"E0.right")])]}),makeQuery(id+"F11.opExtrude","SWEPT_FACE",FACE,{"disambiguationData":[OSD([sQuery(id+"F10.wireOp",EDGE,"E9.1.0")])]})]});
            chamfer(context, id + "F12", {"entities" : qUnion([Q0, Q1, Q2, Q3, Q4, Q5, Q6, Q7, Q8, Q9, Q10, Q11, Q12, Q13, Q14, Q15, Q16, Q17, Q18, Q19, Q20, Q21, Q22, Q23, Q24, Q25, Q26, Q27, Q28, Q29, Q30, Q31, Q32, Q33, Q34, Q35, Q36, Q37, Q38, Q39, Q40, Q41, Q42, Q43, Q44, Q45, Q46, Q47, Q48, Q49, Q50, Q51, Q52, Q53, Q54, Q55, Q56, Q57, Q58]), "width" : 1.27 * mm, "tangentPropagation" : true});
        }
        {
            var Q0;
            Q0=makeQuery(id+"F1.opRevolve","SWEPT_FACE",FACE,{"disambiguationData":[OSD([sQuery(id+"F0.wireOp",EDGE,"E0.top")])]});
            var sketch = newSketch(context, id + "F13", { "sketchPlane" : qUnion([Q0])});
            skCircle(sketch, "E10", {"center": v(0, 0) * mm, "radius": 22.4 * mm});
            skSolve(sketch);
        }
        {
            var Q0;
            Q0=makeQuery(id+"F13.imprint","IMPRINT",FACE,{"disambiguationData":[TD([[makeQuery(id+"F13.imprint","IMPRINT",EDGE,{"derivedFrom":sQuery(id+"F13.wireOp",EDGE,"E10")}),1.0]])]});
            extrude(context, id + "F14", {"entities" : qUnion([Q0]), "operationType" : NewBodyOperationType.REMOVE, "oppositeDirection" : true, "depth" : 4.06 * mm, "offsetDistance" : 25.4 * mm});
        }
        {
            var Q0;
            Q0=qCreatedBy(makeId("Front.planeOp"),FACE);
            var sketch = newSketch(context, id + "F15", { "sketchPlane" : qUnion([Q0])});
            skCircle(sketch, "E11", {"center": v(40.74, 0) * mm, "radius": 27.62 * mm});
            skSolve(sketch);
        }
        {
            var Q0;
            Q0 = qSketchRegion(id + "F15", true);
            var Q1;
            Q1=makeQuery(id+"F3.opExtrude","SWEPT_FACE",FACE,{"disambiguationData":[OSD([sQuery(id+"F2.wireOp",EDGE,"E3")])]});
            revolve(context, id + "F16", {"operationType" : NewBodyOperationType.REMOVE, "surfaceOperationType" : NewSurfaceOperationType.NEW, "entities" : qUnion([Q0]), "axis" : qUnion([Q1]), "revolveType" : RevolveType.FULL, "oppositeDirection" : true});
        }
    });
